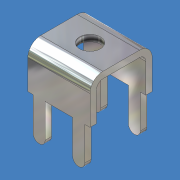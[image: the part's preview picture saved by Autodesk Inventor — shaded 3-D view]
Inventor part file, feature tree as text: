
AUTODESK INVENTOR PART (.ipt)
format: ipt  version: 2011 SP1 (Build 150282100, 282)  size: 171,520 bytes
history: native  units: mm (DEFAULTED — no unit token found)
features: sheet_metal_op x13, sketch x8, other x7, hole x1, chamfer x1
ambient origin geometry x8: Origin, YZ Plane, XZ Plane, XY Plane, X Axis, Y Axis, Z Axis, Center Point
bodies: Solid1 (feature_tree)
feature tree (30):
  sheet_metal_op  "Face1"
  sheet_metal_op  "Flange1"
  sheet_metal_op  "Flange2"
  hole  "Hole1"  [1 undecoded]
  sheet_metal_op  "Flange3"
  sheet_metal_op  "Flange4"
  sheet_metal_op  "Flange5"
  sheet_metal_op  "Flange6"
  chamfer  "Corner Round1"
  sketch  "Sketch1"  dims[d0=7.874mm d1=7.874mm]
  other  "Plate1"
  sketch  "Sketch2"  dims[d2=0.8128mm]
  other  "Plate2"
  sheet_metal_op  "Bend1"
  sketch  "Sketch3"  dims[d3=0.8128mm]
  other  "Plate3"
  sheet_metal_op  "Bend2"
  sketch  "Sketch4"  dims[d4=5.334mm d5=90.0deg d6=0.8128mm]
  sketch  "Sketch5"  dims[d7=0.8128mm]
  other  "Plate4"
  sheet_metal_op  "Bend3"
  sketch  "Sketch6"  dims[d8=5.334mm d9=90.0deg d10=0.8128mm]
  other  "Plate5"
  sheet_metal_op  "Bend4"
  sketch  "Sketch7"  dims[d11=2.6416mm d12=12.7mm d13=9.525mm d14=6.35mm d15=14.3117mm d16=19.05mm d17=20.594885mm]
  other  "Plate6"
  sheet_metal_op  "Bend5"
  sketch  "Sketch8"  dims[d18=0.6731mm d19=1.524mm d20=0.8128mm d21=5.0038mm d22=0.0mm d23=0.8128mm d25=0.6731mm d26=1.524mm d27=0.8128mm d28=5.0038mm d29=0.0mm d30=0.8128mm d31=0.6731mm d32=1.524mm d33=0.8128mm d34=5.0038mm d35=0.0mm d36=0.8128mm d37=0.6731mm d38=1.524mm d39=0.8128mm d40=5.0038mm d41=0.0mm d42=0.8128mm d43=0.762mm d44=0.8128mm d45=0.4064mm d46=1.6256mm d47=0.8128mm d48=0.4064mm d49=1.6256mm d50=0.8128mm d51=0.4064mm d52=1.6256mm d53=0.8128mm d54=0.4064mm d55=1.6256mm d56=0.8128mm d57=0.4064mm d58=1.6256mm d59=0.8128mm d60=0.4064mm d61=1.6256mm]
  other  "Plate7"
  sheet_metal_op  "Bend6"
note: 1 required parameter value undecoded (feature->parameter linkage not recoverable at this tier; creation-order binding heuristic only, values carry confidence <= 0.55)
